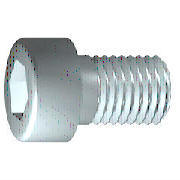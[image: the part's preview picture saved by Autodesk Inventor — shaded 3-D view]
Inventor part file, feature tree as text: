
AUTODESK INVENTOR PART (.ipt)
format: ipt  version: 2014 (Build 180170000, 170)  size: 198,656 bytes
history: native  units: mm (DEFAULTED — no unit token found)
features: sketch x2, extrude x1, plane x1, fillet x1
ambient origin geometry x7: Origin, YZ Plane, XY Plane, X Axis, Y Axis, Z Axis, Center Point
bodies: Solid1 (feature_tree), Body (feature_tree)
feature tree (5):
  extrude  "Slot"  Depth=3.5052mm
  plane  "Work Plane1"
  fillet  "Fillet2"  Radius=3.5052mm
  sketch  "Sketch1"  dims[d1=7.540552mm d2=1.984348mm d3=3.5052mm]
  sketch  "Sketch2"  dims[d4=1.6256mm d5=60.0deg d6=3.5052mm d7=3.5052mm d8=3.196904mm d9=5.7404mm d10=90.0deg d11=10.0mm d12=0.0mm d13=7.540552mm d14=0.0mm d15=0.47244mm d16=0.47244mm d17=0.3302mm d19=0.0mm d26=9.525mm d27=45.0deg d28=0.0mm d29=0.0mm d30=0.127mm]
